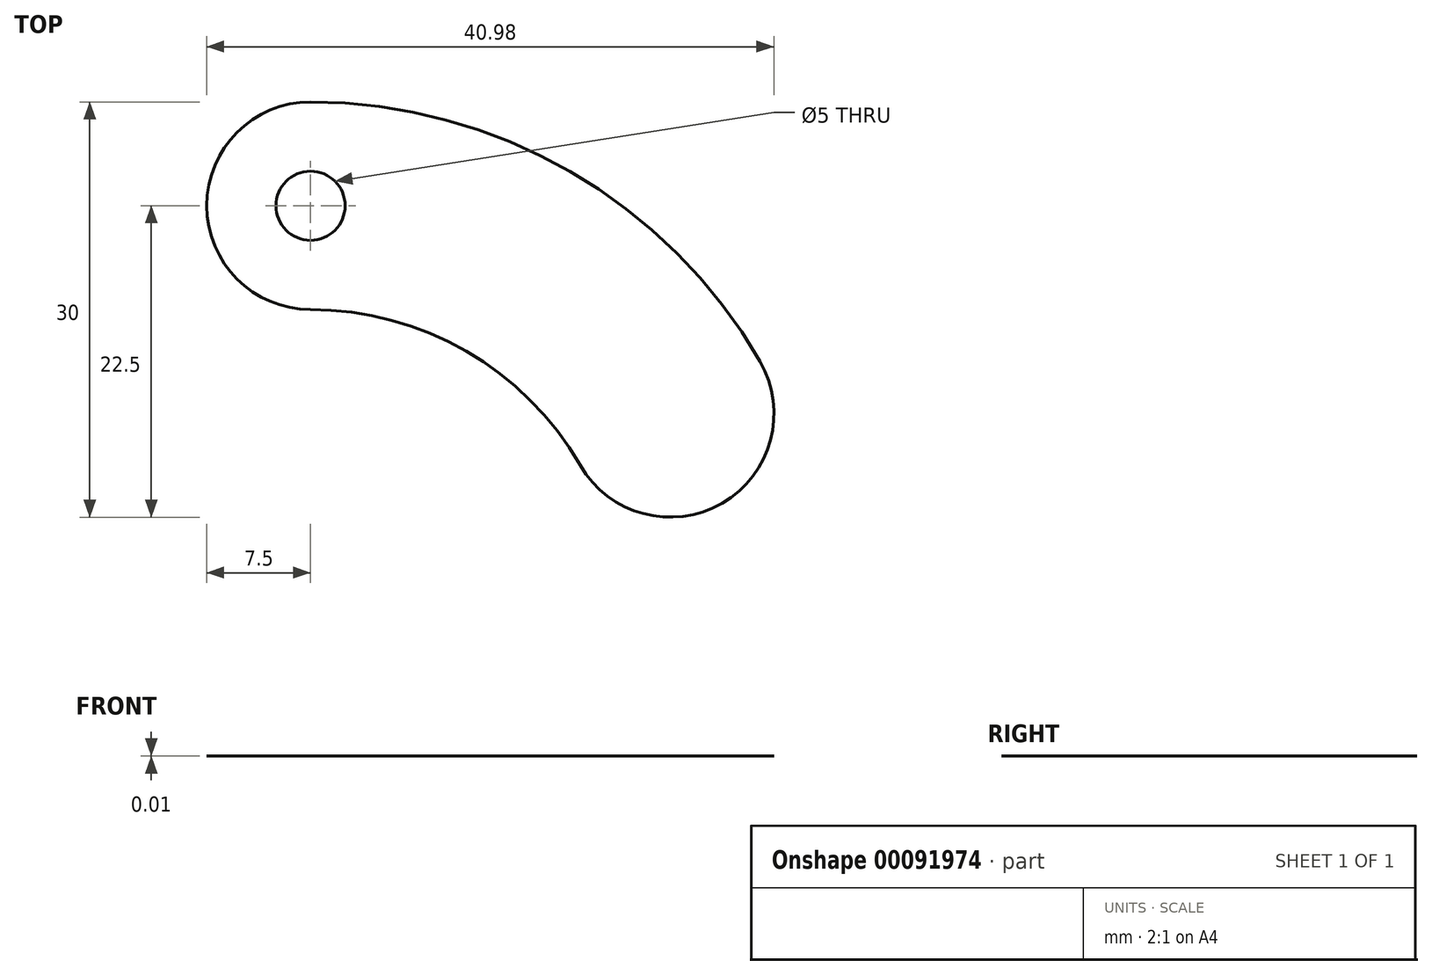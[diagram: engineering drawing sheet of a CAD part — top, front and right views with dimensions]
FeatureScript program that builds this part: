
annotation { "Feature Type Name" : "Feature", "Feature Type Description" : "" }
export const myFeature = defineFeature(function(context is Context, id is Id, definition is map)
    precondition{}
    {
        {
            var Q0;
            Q0=qCreatedBy(makeId("Top.planeOp"),FACE);
            var sketch = newSketch(context, id + "F0", { "sketchPlane" : qUnion([Q0])});
            skCircle(sketch, "E0", {"center": v(0, 0) * mm, "radius": 2.5 * mm});
            skCircle(sketch, "E1", {"center": v(0, 0) * mm, "radius": 30 * mm, "construction": true});
            skArc(sketch, "E2", {"start": v(0, 0) * mm, "mid": v(15, -4.02) * mm, "end": v(25.98, -15) * mm});
            skArc(sketch, "E3.0.startCap", {"start": v(0, -7.5) * mm, "mid": v(-7.5, 0) * mm, "end": v(0, 7.5) * mm});
            skArc(sketch, "E3.0.endCap", {"start": v(32.48, -11.25) * mm, "mid": v(29.73, -21.5) * mm, "end": v(19.49, -18.75) * mm});
            skArc(sketch, "E3.0.left", {"start": v(0, 7.5) * mm, "mid": v(18.75, 2.48) * mm, "end": v(32.48, -11.25) * mm});
            skArc(sketch, "E3.0.right", {"start": v(0, -7.5) * mm, "mid": v(11.25, -10.51) * mm, "end": v(19.49, -18.75) * mm});
            skSolve(sketch);
        }
        {
            var Q0;
            Q0=makeQuery(id+"F0.imprint","IMPRINT",FACE,{"disambiguationData":[TD([[makeQuery(id+"F0.imprint","IMPRINT",EDGE,{"derivedFrom":sQuery(id+"F0.wireOp",EDGE,"E0")}),-1.0]])]});
            extrude(context, id + "F1", {"entities" : qUnion([Q0]), "depth" : 1 / 101.6 * mm});
        }
    });
